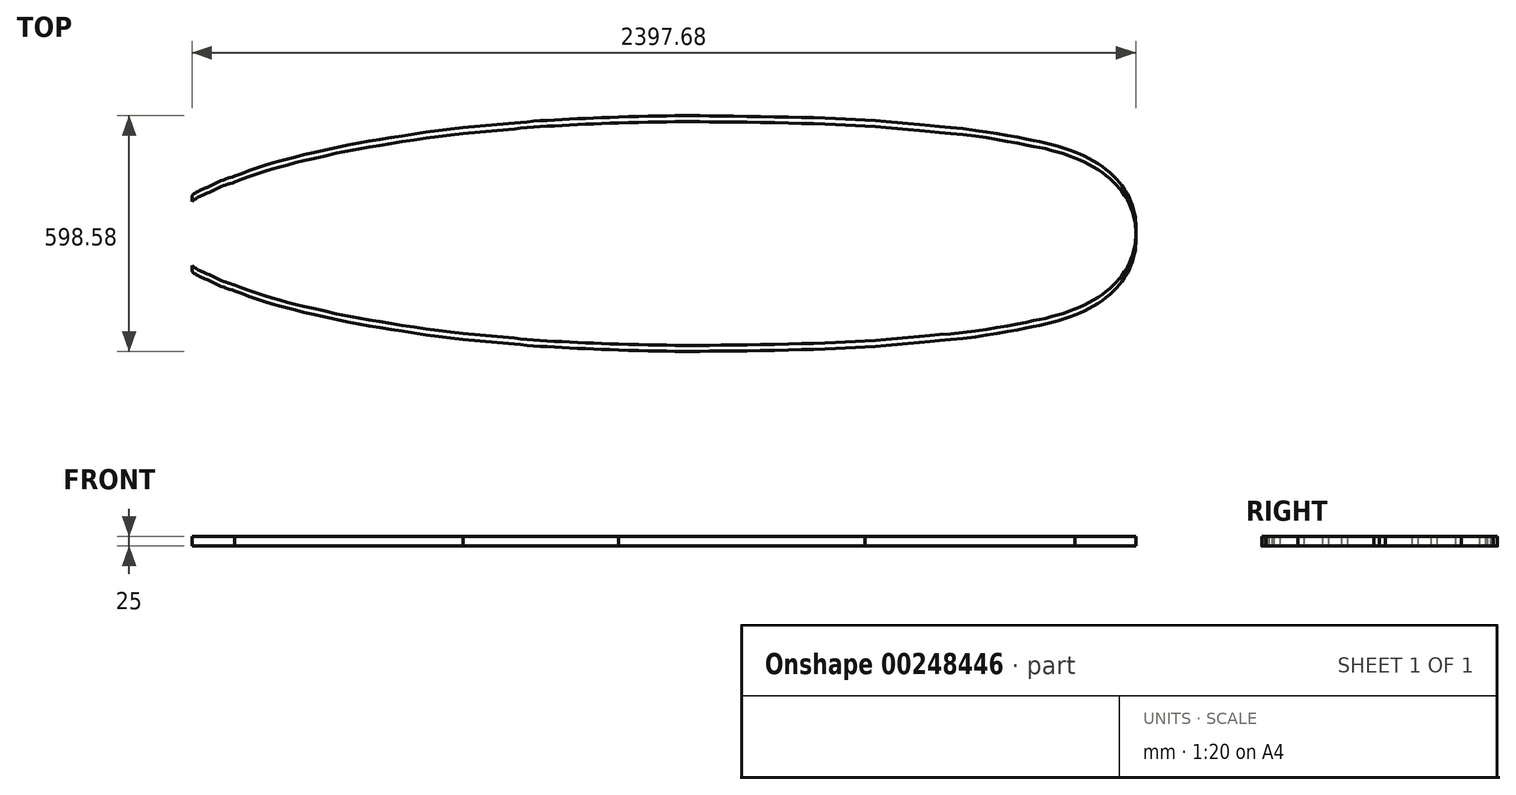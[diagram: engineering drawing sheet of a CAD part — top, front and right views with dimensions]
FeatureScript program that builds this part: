
annotation { "Feature Type Name" : "Feature", "Feature Type Description" : "" }
export const myFeature = defineFeature(function(context is Context, id is Id, definition is map)
    precondition{}
    {
        {
            var Q0;
            Q0=qCreatedBy(makeId("Top.planeOp"),FACE);
            var sketch = newSketch(context, id + "F0", { "sketchPlane" : qUnion([Q0])});
            skFitSpline(sketch, "E0", {"points": [v(4572.5, 526.74) * mm, v(4571.86, 509.8) * mm, v(4569.85, 493.74) * mm, v(4564.4, 472.79) * mm, v(4557.22, 453.27) * mm, v(4541.22, 425.42) * mm, v(4526.16, 406.9) * mm, v(4505.61, 386.63) * mm, v(4481, 366.94) * mm, v(4449.37, 348.93) * mm, v(4418.24, 334.47) * mm], "startDerivative": vector(-4.36, -212.72) * mm, "endDerivative": vector(-267.93, -120.02) * mm});
            skFitSpline(sketch, "E1", {"points": [v(4418.24, 334.47) * mm, v(4403.11, 329.32) * mm, v(4385.32, 323.04) * mm, v(4369.62, 318.15) * mm, v(4353.22, 314.32) * mm, v(4336.12, 309.43) * mm, v(4319.37, 306.64) * mm, v(4297.39, 302.1) * mm, v(4260.75, 295.12) * mm, v(4211.9, 286.4) * mm, v(4158.52, 278.73) * mm, v(4088.63, 270.86) * mm, v(4043.92, 267.35) * mm, v(3989.57, 262.1) * mm, v(3934.34, 256.83) * mm, v(3884.36, 253.32) * mm], "startDerivative": vector(-320.86, -107.7) * mm, "endDerivative": vector(-608.26, -38.86) * mm});
            skFitSpline(sketch, "E2", {"points": [v(3884.36, 253.32) * mm, v(3729.94, 247.06) * mm, v(3490.32, 242.88) * mm, v(3386.04, 242.88) * mm, v(3257.85, 245.78) * mm], "startDerivative": vector(-556.24, -26.96) * mm, "endDerivative": vector(-593.13, 15.55) * mm});
            skFitSpline(sketch, "E3", {"points": [v(3257.85, 245.78) * mm, v(3074.47, 254.38) * mm, v(2958.14, 264.13) * mm, v(2863.56, 272.83) * mm], "startDerivative": vector(-486.59, 18.91) * mm, "endDerivative": vector(-327.09, 29.83) * mm});
            skFitSpline(sketch, "E4", {"points": [v(2863.56, 272.83) * mm, v(2750.57, 287.15) * mm, v(2651.76, 303.05) * mm, v(2565.43, 317.82) * mm, v(2472.56, 338.8) * mm, v(2416.05, 352.43) * mm, v(2369.96, 365.65) * mm, v(2324.84, 380.04) * mm, v(2283.3, 396.14) * mm], "startDerivative": vector(-727.62, 85.49) * mm, "endDerivative": vector(-416.83, 168.93) * mm});
            skFitSpline(sketch, "E5", {"points": [v(2283.3, 396.14) * mm, v(2251.62, 406.53) * mm, v(2224.1, 419.5) * mm, v(2200.21, 429.9) * mm, v(2184.11, 438.2) * mm, v(2174.82, 444.95) * mm], "startDerivative": vector(-134.96, 39.06) * mm, "endDerivative": vector(-61.49, 47.96) * mm});
            skLineSegment(sketch, "E6", {"start": v(2174.82, 526.74) * mm, "end": v(2174.82, 444.95) * mm});
            skFitSpline(sketch, "E7.MirrorCS", {"points": [v(4418.24, 719.02) * mm, v(4403.11, 724.16) * mm, v(4385.32, 730.44) * mm, v(4369.62, 735.33) * mm, v(4353.22, 739.17) * mm, v(4336.12, 744.05) * mm, v(4319.37, 746.84) * mm, v(4297.39, 751.38) * mm, v(4260.75, 758.36) * mm, v(4211.9, 767.08) * mm, v(4158.52, 774.76) * mm, v(4088.63, 782.63) * mm, v(4043.92, 786.13) * mm, v(3989.57, 791.4) * mm, v(3934.34, 796.65) * mm, v(3884.36, 800.16) * mm], "startDerivative": vector(-320.86, 107.7) * mm, "endDerivative": vector(-608.26, 38.86) * mm});
            skFitSpline(sketch, "E8.MirrorCS", {"points": [v(4572.5, 526.74) * mm, v(4571.86, 543.67) * mm, v(4569.85, 559.74) * mm, v(4564.4, 580.7) * mm, v(4557.22, 600.2) * mm, v(4541.22, 628.06) * mm, v(4526.16, 646.6) * mm, v(4505.61, 666.85) * mm, v(4481, 686.54) * mm, v(4449.37, 704.55) * mm, v(4418.24, 719.02) * mm], "startDerivative": vector(-4.36, 212.72) * mm, "endDerivative": vector(-267.93, 120.02) * mm});
            skFitSpline(sketch, "E9.MirrorCS", {"points": [v(3884.36, 800.16) * mm, v(3729.94, 806.43) * mm, v(3490.32, 810.6) * mm, v(3386.04, 810.6) * mm, v(3257.85, 807.7) * mm], "startDerivative": vector(-556.24, 26.96) * mm, "endDerivative": vector(-593.13, -15.55) * mm});
            skFitSpline(sketch, "E10.MirrorCS", {"points": [v(3257.85, 807.7) * mm, v(3074.47, 799.1) * mm, v(2958.14, 789.35) * mm, v(2863.56, 780.65) * mm], "startDerivative": vector(-486.59, -18.91) * mm, "endDerivative": vector(-327.09, -29.83) * mm});
            skFitSpline(sketch, "E11.MirrorCS", {"points": [v(2863.56, 780.65) * mm, v(2750.57, 766.33) * mm, v(2651.76, 750.43) * mm, v(2565.43, 735.66) * mm, v(2472.56, 714.68) * mm, v(2416.05, 701.06) * mm, v(2369.96, 687.83) * mm, v(2324.84, 673.44) * mm, v(2283.3, 657.34) * mm], "startDerivative": vector(-727.62, -85.49) * mm, "endDerivative": vector(-416.83, -168.93) * mm});
            skFitSpline(sketch, "E12.MirrorCS", {"points": [v(2283.3, 657.34) * mm, v(2251.62, 646.95) * mm, v(2224.1, 633.97) * mm, v(2200.21, 623.59) * mm, v(2184.11, 615.28) * mm, v(2174.82, 608.53) * mm], "startDerivative": vector(-134.96, -39.06) * mm, "endDerivative": vector(-61.49, -47.96) * mm});
            skLineSegment(sketch, "E13.MirrorCS", {"start": v(2174.82, 526.74) * mm, "end": v(2174.82, 608.53) * mm});
            skFitSpline(sketch, "E14", {"points": [v(1680.08, -556.57) * mm, v(1679.45, -573.5) * mm, v(1677.44, -589.57) * mm, v(1671.98, -610.52) * mm, v(1664.8, -630.04) * mm, v(1648.8, -657.9) * mm, v(1633.75, -676.42) * mm, v(1613.2, -696.68) * mm, v(1588.6, -716.37) * mm, v(1556.96, -734.38) * mm, v(1525.82, -748.84) * mm], "startDerivative": vector(-4.36, -212.72) * mm, "endDerivative": vector(-267.93, -120.02) * mm});
            skFitSpline(sketch, "E15", {"points": [v(1525.82, -748.84) * mm, v(1510.7, -754) * mm, v(1492.9, -760.27) * mm, v(1477.2, -765.16) * mm, v(1460.8, -769) * mm, v(1443.7, -773.88) * mm, v(1426.96, -776.67) * mm, v(1404.98, -781.2) * mm, v(1368.34, -788.19) * mm, v(1319.5, -796.9) * mm, v(1266.1, -804.59) * mm, v(1196.22, -812.45) * mm, v(1151.5, -815.96) * mm, v(1097.15, -821.22) * mm, v(1041.92, -826.48) * mm, v(991.95, -829.99) * mm], "startDerivative": vector(-320.86, -107.7) * mm, "endDerivative": vector(-608.26, -38.86) * mm});
            skFitSpline(sketch, "E16", {"points": [v(991.95, -829.99) * mm, v(837.52, -836.25) * mm, v(597.9, -840.43) * mm, v(493.62, -840.43) * mm, v(365.44, -837.53) * mm], "startDerivative": vector(-556.24, -26.96) * mm, "endDerivative": vector(-593.13, 15.55) * mm});
            skFitSpline(sketch, "E17", {"points": [v(365.44, -837.53) * mm, v(182.06, -828.93) * mm, v(65.73, -819.18) * mm, v(-28.85, -810.48) * mm], "startDerivative": vector(-486.59, 18.91) * mm, "endDerivative": vector(-327.09, 29.83) * mm});
            skFitSpline(sketch, "E18", {"points": [v(-28.85, -810.48) * mm, v(-141.84, -796.16) * mm, v(-240.66, -780.26) * mm, v(-326.98, -765.5) * mm, v(-419.85, -744.51) * mm, v(-476.36, -730.89) * mm, v(-522.46, -717.66) * mm, v(-567.57, -703.27) * mm, v(-609.12, -687.17) * mm], "startDerivative": vector(-727.62, 85.49) * mm, "endDerivative": vector(-416.83, 168.93) * mm});
            skFitSpline(sketch, "E19", {"points": [v(-609.12, -687.17) * mm, v(-640.8, -676.78) * mm, v(-668.32, -663.8) * mm, v(-692.2, -653.42) * mm, v(-708.3, -645.1) * mm, v(-717.59, -638.36) * mm], "startDerivative": vector(-134.96, 39.06) * mm, "endDerivative": vector(-61.49, 47.96) * mm});
            skLineSegment(sketch, "E20", {"start": v(-717.59, -556.57) * mm, "end": v(-717.59, -638.36) * mm});
            skFitSpline(sketch, "E21.MirrorCS", {"points": [v(1525.82, -364.3) * mm, v(1510.7, -359.15) * mm, v(1492.9, -352.87) * mm, v(1477.2, -347.98) * mm, v(1460.8, -344.14) * mm, v(1443.7, -339.26) * mm, v(1426.96, -336.47) * mm, v(1404.98, -331.93) * mm, v(1368.34, -324.95) * mm, v(1319.5, -316.23) * mm, v(1266.1, -308.55) * mm, v(1196.22, -300.69) * mm, v(1151.5, -297.18) * mm, v(1097.15, -291.92) * mm, v(1041.92, -286.66) * mm, v(991.95, -283.15) * mm], "startDerivative": vector(-320.86, 107.7) * mm, "endDerivative": vector(-608.26, 38.86) * mm});
            skFitSpline(sketch, "E22.MirrorCS", {"points": [v(1680.08, -556.57) * mm, v(1679.45, -539.64) * mm, v(1677.44, -523.57) * mm, v(1671.98, -502.62) * mm, v(1664.8, -483.1) * mm, v(1648.8, -455.25) * mm, v(1633.75, -436.72) * mm, v(1613.2, -416.46) * mm, v(1588.6, -396.77) * mm, v(1556.96, -378.76) * mm, v(1525.82, -364.3) * mm], "startDerivative": vector(-4.36, 212.72) * mm, "endDerivative": vector(-267.93, 120.02) * mm});
            skFitSpline(sketch, "E23.MirrorCS", {"points": [v(991.95, -283.15) * mm, v(837.52, -276.89) * mm, v(597.9, -272.7) * mm, v(493.62, -272.7) * mm, v(365.44, -275.6) * mm], "startDerivative": vector(-556.24, 26.96) * mm, "endDerivative": vector(-593.13, -15.55) * mm});
            skFitSpline(sketch, "E24.MirrorCS", {"points": [v(365.44, -275.6) * mm, v(182.06, -284.2) * mm, v(65.73, -293.96) * mm, v(-28.85, -302.66) * mm], "startDerivative": vector(-486.59, -18.91) * mm, "endDerivative": vector(-327.09, -29.83) * mm});
            skFitSpline(sketch, "E25.MirrorCS", {"points": [v(-28.85, -302.66) * mm, v(-141.84, -316.98) * mm, v(-240.66, -332.88) * mm, v(-326.98, -347.65) * mm, v(-419.85, -368.63) * mm, v(-476.36, -382.25) * mm, v(-522.46, -395.48) * mm, v(-567.57, -409.87) * mm, v(-609.12, -425.97) * mm], "startDerivative": vector(-727.62, -85.49) * mm, "endDerivative": vector(-416.83, -168.93) * mm});
            skFitSpline(sketch, "E26.MirrorCS", {"points": [v(-609.12, -425.97) * mm, v(-640.8, -436.36) * mm, v(-668.32, -449.34) * mm, v(-692.2, -459.72) * mm, v(-708.3, -468.03) * mm, v(-717.59, -474.78) * mm], "startDerivative": vector(-134.96, -39.06) * mm, "endDerivative": vector(-61.49, -47.96) * mm});
            skLineSegment(sketch, "E27.MirrorCS", {"start": v(-717.59, -556.57) * mm, "end": v(-717.59, -474.78) * mm});
            skFitSpline(sketch, "E28.MirrorCS", {"points": [v(1525.82, -349.2) * mm, v(1510.7, -344.05) * mm, v(1492.9, -337.77) * mm, v(1477.2, -332.88) * mm, v(1460.8, -329.05) * mm, v(1443.7, -324.16) * mm, v(1426.96, -321.37) * mm, v(1404.98, -316.83) * mm, v(1368.34, -309.86) * mm, v(1319.5, -301.13) * mm, v(1266.1, -293.46) * mm, v(1196.22, -285.59) * mm, v(1151.5, -282.08) * mm, v(1097.15, -276.82) * mm, v(1041.92, -271.56) * mm, v(991.95, -268.05) * mm], "startDerivative": vector(-320.86, 107.7) * mm, "endDerivative": vector(-608.26, 38.86) * mm});
            skFitSpline(sketch, "E29.MirrorCS", {"points": [v(1680.1, -541.47) * mm, v(1679.45, -524.54) * mm, v(1677.44, -508.47) * mm, v(1671.98, -487.52) * mm, v(1664.8, -468) * mm, v(1648.8, -440.15) * mm, v(1633.75, -421.62) * mm, v(1613.2, -401.36) * mm, v(1588.6, -381.68) * mm, v(1556.96, -363.66) * mm, v(1525.82, -349.2) * mm], "startDerivative": vector(-4.36, 212.72) * mm, "endDerivative": vector(-267.93, 120.02) * mm});
            skFitSpline(sketch, "E30.MirrorCS", {"points": [v(991.95, -268.05) * mm, v(837.52, -261.79) * mm, v(597.9, -257.61) * mm, v(493.62, -257.61) * mm, v(365.44, -260.5) * mm], "startDerivative": vector(-556.24, 26.96) * mm, "endDerivative": vector(-593.13, -15.55) * mm});
            skFitSpline(sketch, "E31.MirrorCS", {"points": [v(365.44, -260.5) * mm, v(182.06, -269.1) * mm, v(65.73, -278.86) * mm, v(-28.85, -287.56) * mm], "startDerivative": vector(-486.59, -18.91) * mm, "endDerivative": vector(-327.09, -29.83) * mm});
            skFitSpline(sketch, "E32.MirrorCS", {"points": [v(-28.85, -287.56) * mm, v(-141.84, -301.88) * mm, v(-240.66, -317.78) * mm, v(-326.98, -332.55) * mm, v(-419.85, -353.53) * mm, v(-476.36, -367.16) * mm, v(-522.46, -380.38) * mm, v(-567.57, -394.78) * mm, v(-609.12, -410.87) * mm], "startDerivative": vector(-727.62, -85.49) * mm, "endDerivative": vector(-416.83, -168.93) * mm});
            skFitSpline(sketch, "E33.MirrorCS", {"points": [v(-609.12, -410.87) * mm, v(-640.8, -421.26) * mm, v(-668.32, -434.24) * mm, v(-692.2, -444.63) * mm, v(-708.3, -452.94) * mm, v(-717.59, -459.69) * mm], "startDerivative": vector(-134.96, -39.06) * mm, "endDerivative": vector(-61.49, -47.96) * mm});
            skLineSegment(sketch, "E34.MirrorCS", {"start": v(-717.59, -541.47) * mm, "end": v(-717.59, -459.69) * mm});
            skLineSegment(sketch, "E35", {"start": v(-717.59, -556.57) * mm, "end": v(1680.08, -556.57) * mm});
            skLineSegment(sketch, "E36.MirrorCS", {"start": v(-717.59, -571.67) * mm, "end": v(-717.59, -653.45) * mm});
            skFitSpline(sketch, "E37.MirrorCS", {"points": [v(-609.12, -702.27) * mm, v(-640.8, -691.88) * mm, v(-668.32, -678.9) * mm, v(-692.2, -668.51) * mm, v(-708.3, -660.2) * mm, v(-717.59, -653.45) * mm], "startDerivative": vector(-134.96, 39.06) * mm, "endDerivative": vector(-61.49, 47.96) * mm});
            skFitSpline(sketch, "E38.MirrorCS", {"points": [v(-28.85, -825.58) * mm, v(-141.84, -811.26) * mm, v(-240.66, -795.35) * mm, v(-326.98, -780.59) * mm, v(-419.85, -759.6) * mm, v(-476.36, -745.98) * mm, v(-522.46, -732.76) * mm, v(-567.57, -718.36) * mm, v(-609.12, -702.27) * mm], "startDerivative": vector(-727.62, 85.49) * mm, "endDerivative": vector(-416.83, 168.93) * mm});
            skFitSpline(sketch, "E39.MirrorCS", {"points": [v(365.44, -852.63) * mm, v(182.06, -844.03) * mm, v(65.73, -834.28) * mm, v(-28.85, -825.58) * mm], "startDerivative": vector(-486.59, 18.91) * mm, "endDerivative": vector(-327.09, 29.83) * mm});
            skFitSpline(sketch, "E40.MirrorCS", {"points": [v(991.95, -845.08) * mm, v(837.52, -851.35) * mm, v(597.9, -855.53) * mm, v(493.62, -855.53) * mm, v(365.44, -852.63) * mm], "startDerivative": vector(-556.24, -26.96) * mm, "endDerivative": vector(-593.13, 15.55) * mm});
            skFitSpline(sketch, "E41.MirrorCS", {"points": [v(1525.82, -763.94) * mm, v(1510.7, -769.09) * mm, v(1492.9, -775.37) * mm, v(1477.2, -780.25) * mm, v(1460.8, -784.1) * mm, v(1443.7, -788.98) * mm, v(1426.96, -791.77) * mm, v(1404.98, -796.3) * mm, v(1368.34, -803.28) * mm, v(1319.5, -812) * mm, v(1266.1, -819.68) * mm, v(1196.22, -827.55) * mm, v(1151.5, -831.06) * mm, v(1097.15, -836.32) * mm, v(1041.92, -841.58) * mm, v(991.95, -845.08) * mm], "startDerivative": vector(-320.86, -107.7) * mm, "endDerivative": vector(-608.26, -38.86) * mm});
            skFitSpline(sketch, "E42.MirrorCS", {"points": [v(1680.1, -571.67) * mm, v(1679.45, -588.6) * mm, v(1677.44, -604.67) * mm, v(1671.98, -625.62) * mm, v(1664.8, -645.13) * mm, v(1648.8, -672.99) * mm, v(1633.75, -691.52) * mm, v(1613.2, -711.78) * mm, v(1588.6, -731.46) * mm, v(1556.96, -749.48) * mm, v(1525.82, -763.94) * mm], "startDerivative": vector(-4.36, -212.72) * mm, "endDerivative": vector(-267.93, -120.02) * mm});
            skLineSegment(sketch, "E43", {"start": v(1680.1, -541.47) * mm, "end": v(1680.08, -556.57) * mm});
            skLineSegment(sketch, "E44", {"start": v(1680.1, -571.67) * mm, "end": v(1680.08, -556.57) * mm});
            skSolve(sketch);
        }
        {
            var Q0;
            Q0=makeQuery(id+"F0.imprint","IMPRINT",FACE,{"disambiguationData":[TD([[makeQuery(id+"F0.imprint","IMPRINT",EDGE,{"derivedFrom":sQuery(id+"F0.wireOp",EDGE,"E14")}),1.0]])]});
            var Q1;
            Q1=makeQuery(id+"F0.imprint","IMPRINT",FACE,{"disambiguationData":[TD([[makeQuery(id+"F0.imprint","IMPRINT",EDGE,{"derivedFrom":sQuery(id+"F0.wireOp",EDGE,"E21.MirrorCS")}),-1.0]])]});
            extrude(context, id + "F1", {"entities" : qUnion([Q0, Q1]), "depth" : 25 * mm});
        }
    });
